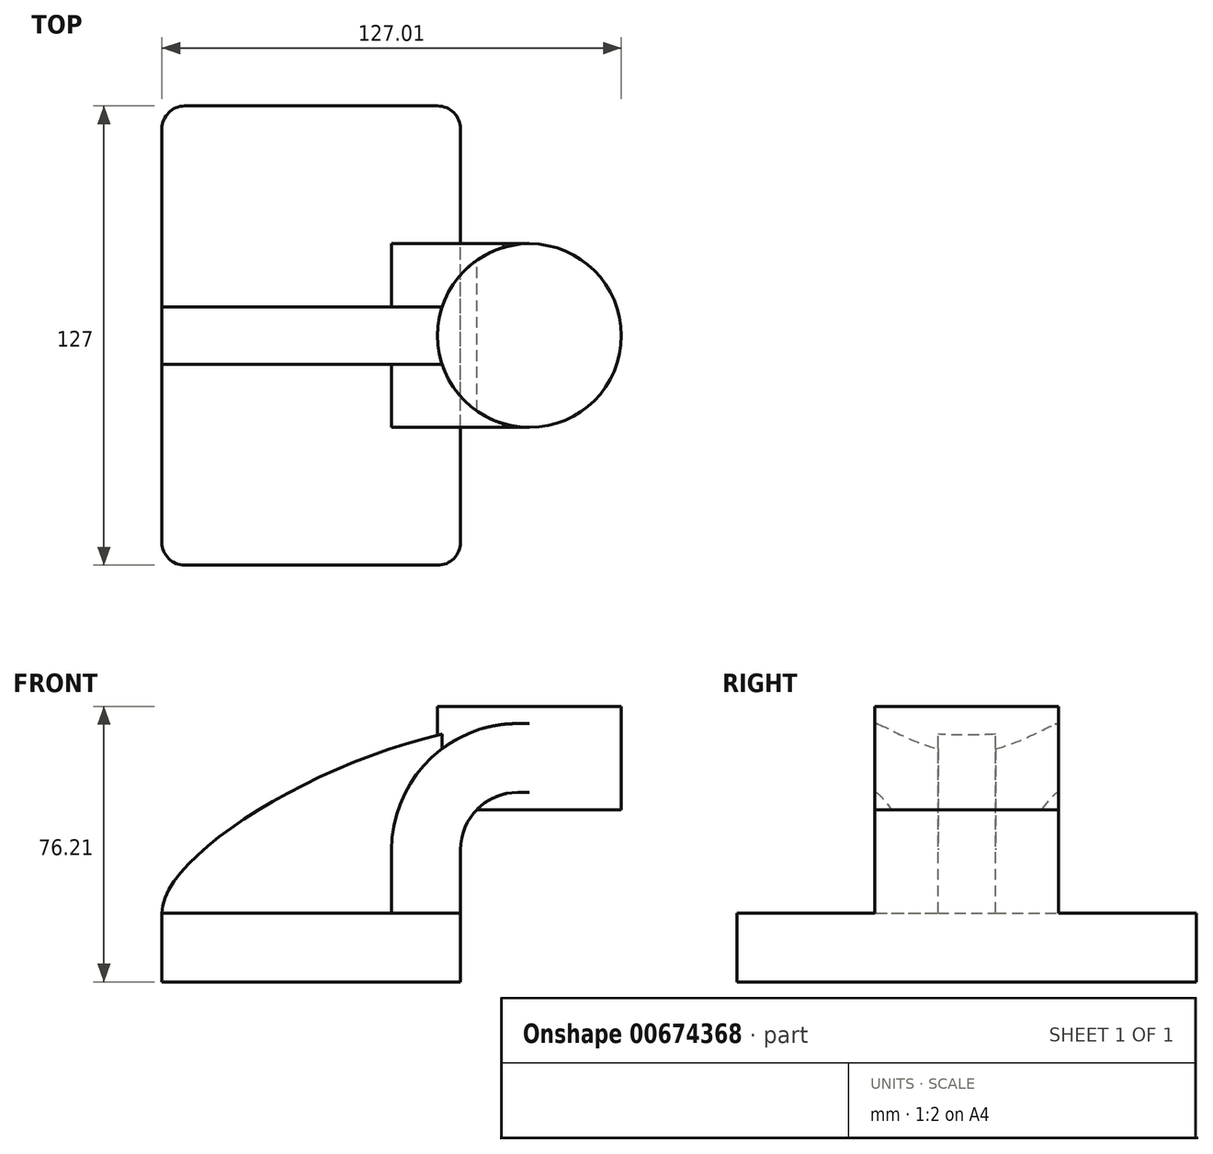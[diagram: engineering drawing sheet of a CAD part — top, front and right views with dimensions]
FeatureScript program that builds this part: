
annotation { "Feature Type Name" : "Feature", "Feature Type Description" : "" }
export const myFeature = defineFeature(function(context is Context, id is Id, definition is map)
    precondition{}
    {
        {
            var Q0;
            Q0=qCreatedBy(makeId("Front.planeOp"),FACE);
            var sketch = newSketch(context, id + "F0", { "sketchPlane" : qUnion([Q0])});
            skLineSegment(sketch, "E0.bottom", {"start": v(-41.28, 9.53) * mm, "end": v(41.28, 9.53) * mm});
            skLineSegment(sketch, "E0.top", {"start": v(-41.28, -9.52) * mm, "end": v(41.28, -9.52) * mm});
            skLineSegment(sketch, "E0.left", {"start": v(-41.28, 9.53) * mm, "end": v(-41.28, -9.52) * mm});
            skLineSegment(sketch, "E0.right", {"start": v(41.28, 9.53) * mm, "end": v(41.28, -9.52) * mm});
            skPoint(sketch, "E0.middle", {"position": v(0, 0) * mm});
            skLineSegment(sketch, "E1.bottom", {"start": v(60.33, 66.68) * mm, "end": v(111.13, 66.68) * mm});
            skLineSegment(sketch, "E1.top", {"start": v(60.33, 38.1) * mm, "end": v(111.13, 38.1) * mm});
            skLineSegment(sketch, "E1.left", {"start": v(60.33, 66.68) * mm, "end": v(60.33, 38.1) * mm});
            skLineSegment(sketch, "E1.right", {"start": v(111.13, 66.68) * mm, "end": v(111.13, 38.1) * mm});
            skPoint(sketch, "E1.middle", {"position": v(85.73, 52.39) * mm});
            skLineSegment(sketch, "E2", {"start": v(41.28, 9.53) * mm, "end": v(41.28, 27) * mm});
            skArc(sketch, "E3", {"start": v(41.28, 27) * mm, "mid": v(45.92, 38.23) * mm, "end": v(57.15, 42.88) * mm});
            skLineSegment(sketch, "E4", {"start": v(57.15, 42.88) * mm, "end": v(65.1, 42.88) * mm});
            skLineSegment(sketch, "E5.0", {"start": v(57.15, 61.93) * mm, "end": v(65.1, 61.93) * mm});
            skArc(sketch, "E5.1", {"start": v(22.23, 27) * mm, "mid": v(32.45, 51.7) * mm, "end": v(57.15, 61.93) * mm});
            skLineSegment(sketch, "E5.2", {"start": v(22.23, 9.53) * mm, "end": v(22.23, 27) * mm});
            skLineSegment(sketch, "E6", {"start": v(65.1, 42.88) * mm, "end": v(85.73, 42.88) * mm});
            skPoint(sketch, "E6.endSnap0", {"position": v(85.73, 38.1) * mm});
            skLineSegment(sketch, "E7", {"start": v(65.1, 61.93) * mm, "end": v(85.73, 61.93) * mm});
            skPoint(sketch, "E7.endSnap0", {"position": v(85.73, 66.68) * mm});
            skLineSegment(sketch, "E8", {"start": v(85.73, 66.68) * mm, "end": v(85.73, 38.1) * mm});
            skFitSpline(sketch, "E9", {"points": [v(-41.28, 9.53) * mm, v(57.15, 61.93) * mm], "startDerivative": vector(-0.75, 54.31) * mm, "endDerivative": vector(124.79, 4.34) * mm});
            skSolve(sketch);
        }
        {
            var Q0;
            Q0=makeQuery(id+"F0.imprint","IMPRINT",FACE,{"disambiguationData":[TD([[makeQuery(id+"F0.imprint","IMPRINT",EDGE,{"derivedFrom":sQuery(id+"F0.wireOp",EDGE,"E0.top")}),1.0]])]});
            extrude(context, id + "F1", {"entities" : qUnion([Q0]), "endBound" : BoundingType.SYMMETRIC, "depth" : 127 * mm, "offsetDistance" : 25.4 * mm});
        }
        {
            var Q0;
            {var subQ1=sQuery(id+"F0.wireOp",EDGE,"E2");Q0=makeQuery(id+"F0.imprint","IMPRINT",FACE,{"disambiguationData":[TD([[makeQuery(id+"F0.imprint","IMPRINT",EDGE,{"derivedFrom":subQ1}),1.0]])]});}
            extrude(context, id + "F2", {"entities" : qUnion([Q0]), "operationType" : NewBodyOperationType.ADD, "endBound" : BoundingType.SYMMETRIC, "depth" : 50.8 * mm, "offsetDistance" : 25.4 * mm});
        }
        {
            var Q0;
            {var subQ3=sQuery(id+"F0.wireOp",EDGE,"E5.2");Q0=makeQuery(id+"F0.imprint","IMPRINT",FACE,{"disambiguationData":[TD([[makeQuery(id+"F0.imprint","IMPRINT",EDGE,{"derivedFrom":subQ3}),1.0]])]});}
            extrude(context, id + "F3", {"entities" : qUnion([Q0]), "operationType" : NewBodyOperationType.ADD, "endBound" : BoundingType.SYMMETRIC, "depth" : 15.88 * mm, "offsetDistance" : 25.4 * mm});
        }
        {
            var Q0;
            {var subQ0=sQuery(id+"F0.wireOp",EDGE,"E7");Q0=makeQuery(id+"F0.imprint","IMPRINT",FACE,{"disambiguationData":[TD([[makeQuery(id+"F0.imprint","IMPRINT",EDGE,{"derivedFrom":subQ0}),1.0]])]});}
            var Q1;
            {var subQ0=sQuery(id+"F0.wireOp",EDGE,"E6");Q1=makeQuery(id+"F0.imprint","IMPRINT",FACE,{"disambiguationData":[TD([[makeQuery(id+"F0.imprint","IMPRINT",EDGE,{"derivedFrom":subQ0}),1.0]])]});}
            var Q2;
            {var subQ0=sQuery(id+"F0.wireOp",EDGE,"E6");Q2=makeQuery(id+"F0.imprint","IMPRINT",FACE,{"disambiguationData":[TD([[makeQuery(id+"F0.imprint","IMPRINT",EDGE,{"derivedFrom":subQ0}),-1.0]])]});}
            var Q3;
            Q3=sQuery(id+"F0.wireOp",EDGE,"E1.left");
            revolve(context, id + "F4", {"operationType" : NewBodyOperationType.ADD, "entities" : qUnion([Q0, Q1, Q2]), "axis" : qUnion([Q3]), "revolveType" : RevolveType.FULL});
        }
        {
            var Q0;
            Q0=makeQuery(id+"F1.opExtrude","CAP_EDGE",EDGE,{"disambiguationData":[OSD([sQuery(id+"F0.wireOp",EDGE,"E0.right")])],"isStart":false});
            var Q1;
            Q1=makeQuery(id+"F1.opExtrude","CAP_EDGE",EDGE,{"disambiguationData":[OSD([sQuery(id+"F0.wireOp",EDGE,"E0.left")])],"isStart":false});
            var Q2;
            Q2=makeQuery(id+"F1.opExtrude","CAP_EDGE",EDGE,{"disambiguationData":[OSD([sQuery(id+"F0.wireOp",EDGE,"E0.right")])],"isStart":true});
            var Q3;
            Q3=makeQuery(id+"F1.opExtrude","CAP_EDGE",EDGE,{"disambiguationData":[OSD([sQuery(id+"F0.wireOp",EDGE,"E0.left")])],"isStart":true});
            fillet(context, id + "F5", {"entities" : qUnion([Q0, Q1, Q2, Q3]), "radius" : 6.35 * mm, "tangentPropagation" : true, "allowEdgeOverflow" : false});
        }
    });
